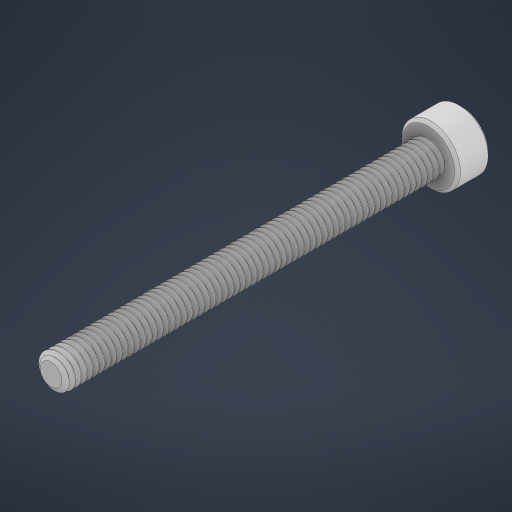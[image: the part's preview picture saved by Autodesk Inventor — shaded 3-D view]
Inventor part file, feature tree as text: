
AUTODESK INVENTOR PART (.ipt)
format: ipt  version: 2023 (Build 270158000, 158)  size: 1,688,064 bytes
history: native  units: in
note: dims shown in document units (in); Inventor stores cm internally (conversion verified against a paired STEP export)
features: chamfer x1
ambient origin geometry x8: Origin, YZ Plane, XZ Plane, XY Plane, X Axis, Y Axis, Z Axis, Center Point
bodies: Solid1 (feature_tree)
feature tree (1):
  chamfer  "Chamfer1"  [1 undecoded]
note: 1 required parameter value undecoded (feature->parameter linkage not recoverable at this tier; creation-order binding heuristic only, values carry confidence <= 0.55)
